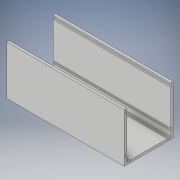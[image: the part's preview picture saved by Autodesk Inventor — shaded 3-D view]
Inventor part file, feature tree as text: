
AUTODESK INVENTOR PART (.ipt)
format: ipt  version: 2017 (Build 210142000, 142)  size: 136,704 bytes
history: native  units: in
note: dims shown in document units (in); Inventor stores cm internally (conversion verified against a paired STEP export)
features: extrude x1, sketch x1
ambient origin geometry x8: Origin, YZ Plane, XZ Plane, XY Plane, X Axis, Y Axis, Z Axis, Center Point
bodies: Solid1 (feature_tree)
feature tree (2):
  extrude  "Extrusion1"  Depth=5.0in
  sketch  "Sketch1"  dims[d0=5.0in d1=5.0in d2=0.25in d3=4.75in d4=4.5in d5=0.125in d9=0.125in d10=0.125in d11=0.125in d12=0.25in d13=0.125in d14=0.125in d15=0.25in d16=0.125in d17=0.125in d18=0.25in d19=12.0in d20=0.0in d21=0.5in d22=0.125in d23=0.25in d24=0.5in d25=0.125in d26=0.25in]
